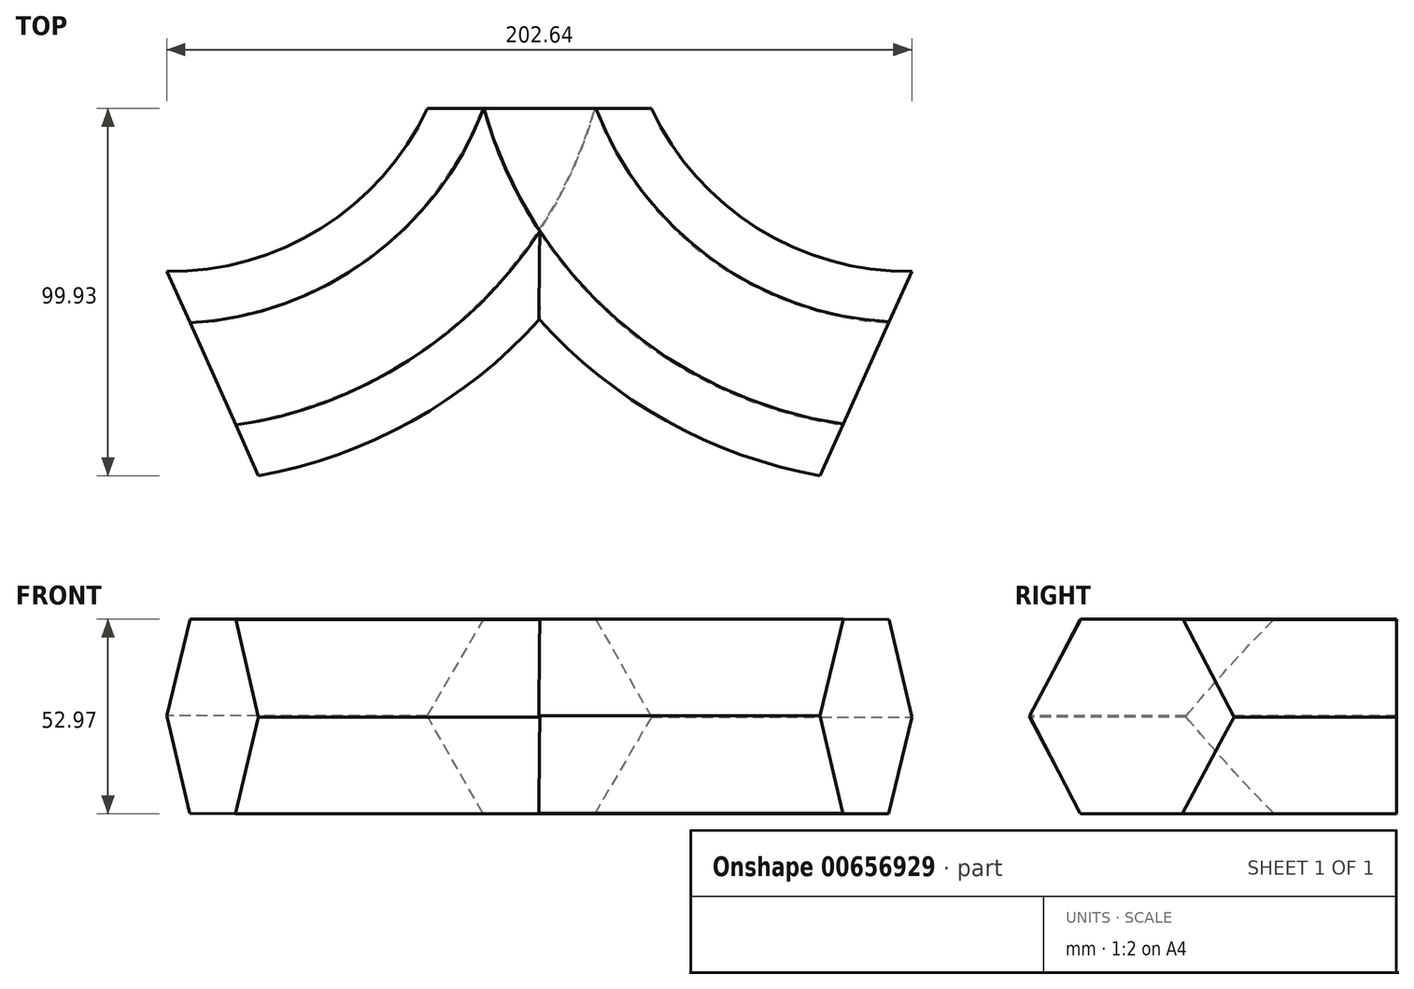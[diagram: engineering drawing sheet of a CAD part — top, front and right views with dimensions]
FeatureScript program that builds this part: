
annotation { "Feature Type Name" : "Feature", "Feature Type Description" : "" }
export const myFeature = defineFeature(function(context is Context, id is Id, definition is map)
    precondition{}
    {
        {
            var Q0;
            Q0=qCreatedBy(makeId("Front.planeOp"),FACE);
            var sketch = newSketch(context, id + "F0", { "sketchPlane" : qUnion([Q0])});
            skCircle(sketch, "E0.cCircle", {"center": v(0, 26.89) * mm, "radius": 26.4 * mm, "construction": true});
            skLineSegment(sketch, "E0.0", {"start": v(-15.4, 0.58) * mm, "end": v(-30.48, 27.07) * mm});
            skLineSegment(sketch, "E0.1", {"start": v(-30.48, 27.07) * mm, "end": v(-15.08, 53.37) * mm});
            skLineSegment(sketch, "E0.2", {"start": v(-15.08, 53.37) * mm, "end": v(15.4, 53.2) * mm});
            skLineSegment(sketch, "E0.3", {"start": v(15.4, 53.2) * mm, "end": v(30.48, 26.7) * mm});
            skLineSegment(sketch, "E0.4", {"start": v(30.48, 26.7) * mm, "end": v(15.08, 0.4) * mm});
            skLineSegment(sketch, "E0.5", {"start": v(15.08, 0.4) * mm, "end": v(-15.4, 0.58) * mm});
            skPoint(sketch, "E0.0.midPoint", {"position": v(-22.94, 13.82) * mm});
            skSolve(sketch);
        }
        {
            var Q0;
            Q0=qCreatedBy(makeId("Top.planeOp"),FACE);
            var sketch = newSketch(context, id + "F1", { "sketchPlane" : qUnion([Q0])});
            skArc(sketch, "E1", {"start": v(-88.86, -72.11) * mm, "mid": v(-33.77, -49.2) * mm, "end": v(0, 0) * mm});
            skArc(sketch, "E2.MirrorCS", {"start": v(88.86, -72.11) * mm, "mid": v(33.77, -49.2) * mm, "end": v(0, 0) * mm});
            skSolve(sketch);
        }
        {
            var Q0;
            Q0 = qSketchRegion(id + "F0", true);
            var Q1;
            Q1=sQuery(id+"F1.wireOp",EDGE,"E2.MirrorCS");
            sweep(context, id + "F2", {"profiles" : qUnion([Q0]), "path" : qUnion([Q1])});
        }
        {
            var Q0;
            Q0=makeQuery(id+"F0.imprint","IMPRINT",FACE,{"disambiguationData":[TD([[makeQuery(id+"F0.imprint","IMPRINT",EDGE,{"derivedFrom":sQuery(id+"F0.wireOp",EDGE,"E0.0")}),-1.0]])]});
            var Q1;
            Q1=sQuery(id+"F1.wireOp",EDGE,"E1");
            sweep(context, id + "F3", {"operationType" : NewBodyOperationType.ADD, "profiles" : qUnion([Q0]), "path" : qUnion([Q1])});
        }
        {
            var Q0;
            Q0=makeQuery(id+"F0.imprint","IMPRINT",FACE,{"disambiguationData":[TD([[makeQuery(id+"F0.imprint","IMPRINT",EDGE,{"derivedFrom":sQuery(id+"F0.wireOp",EDGE,"E0.0")}),-1.0]])]});
            var sketch = newSketch(context, id + "F4", { "sketchPlane" : qUnion([Q0])});
            skCircle(sketch, "E3", {"center": v(0, 27.7) * mm, "radius": 9.73 * mm});
            skSolve(sketch);
        }
    });
